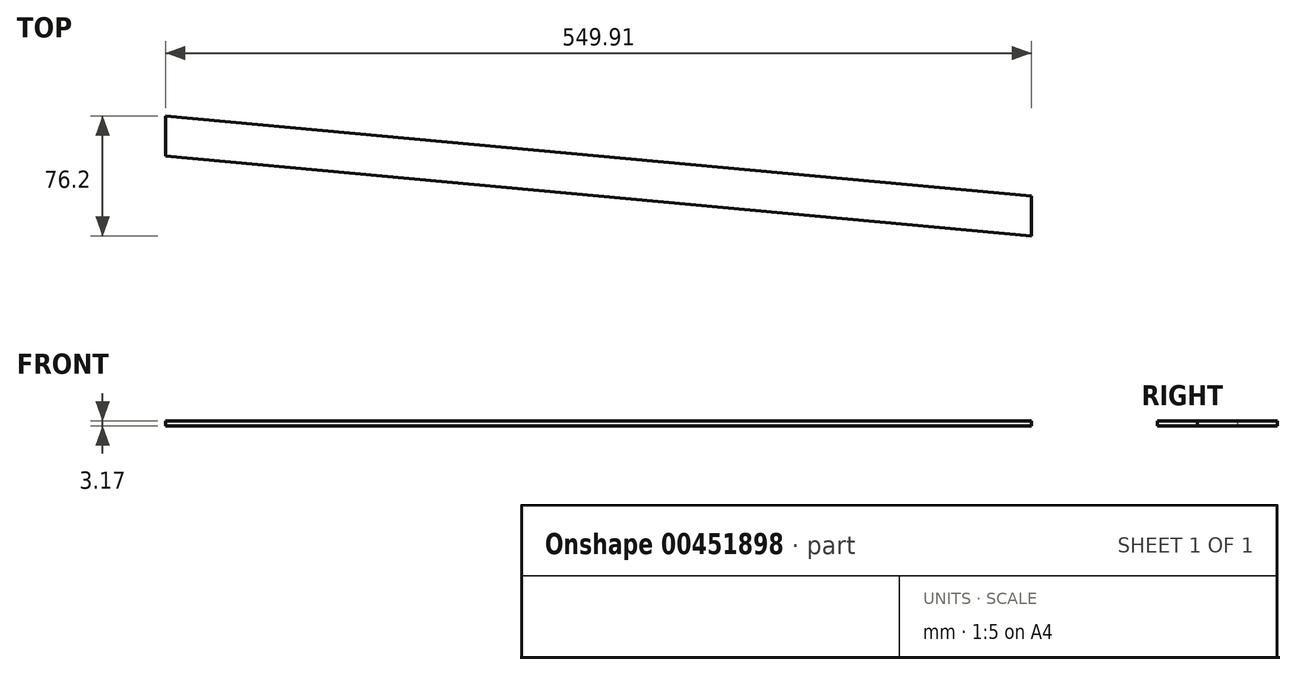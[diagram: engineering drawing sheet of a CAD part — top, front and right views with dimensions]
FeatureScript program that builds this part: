
annotation { "Feature Type Name" : "Feature", "Feature Type Description" : "" }
export const myFeature = defineFeature(function(context is Context, id is Id, definition is map)
    precondition{}
    {
        {
            var Q0;
            Q0=qCreatedBy(makeId("Top.planeOp"),FACE);
            var sketch = newSketch(context, id + "F0", { "sketchPlane" : qUnion([Q0])});
            skLineSegment(sketch, "E0", {"start": v(-200.68, 0.14) * mm, "end": v(-200.68, 139.84) * mm});
            skLineSegment(sketch, "E1", {"start": v(-200.68, 139.84) * mm, "end": v(-195.6, 139.84) * mm});
            skLineSegment(sketch, "E2", {"start": v(-195.6, 139.84) * mm, "end": v(-195.6, 101.74) * mm});
            skLineSegment(sketch, "E3", {"start": v(-195.6, 101.74) * mm, "end": v(460.36, 101.74) * mm, "construction": true});
            skLineSegment(sketch, "E4", {"start": v(-195.6, 101.74) * mm, "end": v(-177.82, 101.74) * mm});
            skLineSegment(sketch, "E5", {"start": v(-200.68, 139.84) * mm, "end": v(460.76, 139.84) * mm, "construction": true});
            skLineSegment(sketch, "E6", {"start": v(-177.82, 101.74) * mm, "end": v(-177.82, 139.84) * mm});
            skLineSegment(sketch, "E7", {"start": v(-177.82, 139.84) * mm, "end": v(-172.74, 139.84) * mm});
            skLineSegment(sketch, "E8", {"start": v(-172.74, 139.84) * mm, "end": v(-172.74, 101.74) * mm});
            skLineSegment(sketch, "E9", {"start": v(-172.74, 101.74) * mm, "end": v(-152.42, 101.74) * mm});
            skLineSegment(sketch, "E10", {"start": v(-152.42, 101.74) * mm, "end": v(-152.42, 139.84) * mm});
            skLineSegment(sketch, "E11", {"start": v(-152.42, 139.84) * mm, "end": v(-147.34, 139.84) * mm});
            skLineSegment(sketch, "E12", {"start": v(-147.34, 139.84) * mm, "end": v(-147.34, 101.74) * mm});
            skLineSegment(sketch, "E13", {"start": v(-147.34, 101.74) * mm, "end": v(-125.75, 101.74) * mm});
            skLineSegment(sketch, "E14", {"start": v(-125.75, 101.74) * mm, "end": v(-125.75, 139.84) * mm});
            skLineSegment(sketch, "E15", {"start": v(-125.75, 139.84) * mm, "end": v(-118.13, 139.84) * mm});
            skLineSegment(sketch, "E16", {"start": v(-118.13, 139.84) * mm, "end": v(-118.13, 101.74) * mm});
            skLineSegment(sketch, "E17", {"start": v(-118.13, 101.74) * mm, "end": v(-96.54, 101.74) * mm});
            skLineSegment(sketch, "E18", {"start": v(-96.54, 101.74) * mm, "end": v(-96.54, 139.84) * mm});
            skLineSegment(sketch, "E19", {"start": v(-96.54, 139.84) * mm, "end": v(-87.65, 139.84) * mm});
            skLineSegment(sketch, "E20", {"start": v(-87.65, 139.84) * mm, "end": v(-87.65, 101.74) * mm});
            skLineSegment(sketch, "E21", {"start": v(-87.65, 101.74) * mm, "end": v(-64.79, 101.74) * mm});
            skLineSegment(sketch, "E22", {"start": v(-64.79, 101.74) * mm, "end": v(-64.79, 139.84) * mm});
            skLineSegment(sketch, "E23", {"start": v(-64.79, 139.84) * mm, "end": v(-54.63, 139.84) * mm});
            skLineSegment(sketch, "E24", {"start": v(-54.63, 139.84) * mm, "end": v(-54.63, 101.74) * mm});
            skLineSegment(sketch, "E25", {"start": v(-54.63, 101.74) * mm, "end": v(-31.77, 101.74) * mm});
            skLineSegment(sketch, "E26", {"start": v(-200.68, 139.84) * mm, "end": v(-200.68, 25.54) * mm, "construction": true});
            skLineSegment(sketch, "E27", {"start": v(-200.68, 25.54) * mm, "end": v(-341.77, 25.54) * mm, "construction": true});
            skLineSegment(sketch, "E28", {"start": v(349.23, -50.66) * mm, "end": v(-200.68, 0.14) * mm});
            skLineSegment(sketch, "E29", {"start": v(-31.77, 101.74) * mm, "end": v(-31.77, 139.84) * mm});
            skLineSegment(sketch, "E30", {"start": v(-31.77, 139.84) * mm, "end": v(-21.6, 139.84) * mm});
            skLineSegment(sketch, "E31", {"start": v(-21.6, 139.84) * mm, "end": v(-21.6, 101.74) * mm});
            skLineSegment(sketch, "E32", {"start": v(-21.6, 101.74) * mm, "end": v(2.52, 101.74) * mm});
            skLineSegment(sketch, "E33", {"start": v(2.52, 101.74) * mm, "end": v(2.52, 139.84) * mm});
            skLineSegment(sketch, "E34", {"start": v(2.52, 139.84) * mm, "end": v(15.22, 139.84) * mm});
            skLineSegment(sketch, "E35", {"start": v(15.22, 139.84) * mm, "end": v(15.22, 101.74) * mm});
            skLineSegment(sketch, "E36", {"start": v(15.22, 101.74) * mm, "end": v(40.62, 101.74) * mm});
            skLineSegment(sketch, "E37", {"start": v(40.62, 101.74) * mm, "end": v(40.62, 139.84) * mm});
            skLineSegment(sketch, "E38", {"start": v(40.62, 139.84) * mm, "end": v(55.86, 139.84) * mm});
            skLineSegment(sketch, "E39", {"start": v(55.86, 139.84) * mm, "end": v(55.86, 101.74) * mm});
            skLineSegment(sketch, "E40", {"start": v(55.86, 101.74) * mm, "end": v(83.8, 101.74) * mm});
            skLineSegment(sketch, "E41", {"start": v(83.8, 101.74) * mm, "end": v(83.8, 139.84) * mm});
            skLineSegment(sketch, "E42", {"start": v(83.8, 139.84) * mm, "end": v(99.04, 139.84) * mm});
            skLineSegment(sketch, "E43", {"start": v(99.04, 139.84) * mm, "end": v(99.04, 101.74) * mm});
            skLineSegment(sketch, "E44", {"start": v(99.04, 101.74) * mm, "end": v(128.25, 101.74) * mm});
            skLineSegment(sketch, "E45", {"start": v(128.25, 101.74) * mm, "end": v(128.25, 139.84) * mm});
            skLineSegment(sketch, "E46", {"start": v(128.25, 139.84) * mm, "end": v(143.5, 139.84) * mm});
            skLineSegment(sketch, "E47", {"start": v(143.5, 139.84) * mm, "end": v(143.5, 101.74) * mm});
            skLineSegment(sketch, "E48", {"start": v(143.5, 101.74) * mm, "end": v(173.97, 101.74) * mm});
            skLineSegment(sketch, "E49", {"start": v(173.97, 101.74) * mm, "end": v(173.97, 139.84) * mm});
            skLineSegment(sketch, "E50", {"start": v(173.97, 139.84) * mm, "end": v(191.75, 139.84) * mm});
            skLineSegment(sketch, "E51", {"start": v(191.75, 139.84) * mm, "end": v(191.75, 101.74) * mm});
            skLineSegment(sketch, "E52", {"start": v(191.75, 101.74) * mm, "end": v(223.5, 101.74) * mm});
            skLineSegment(sketch, "E53", {"start": v(223.5, 101.74) * mm, "end": v(223.5, 139.84) * mm});
            skLineSegment(sketch, "E54", {"start": v(223.5, 139.84) * mm, "end": v(241.28, 139.84) * mm});
            skLineSegment(sketch, "E55", {"start": v(241.28, 139.84) * mm, "end": v(241.28, 101.74) * mm});
            skLineSegment(sketch, "E56", {"start": v(241.28, 101.74) * mm, "end": v(274.3, 101.74) * mm});
            skLineSegment(sketch, "E57", {"start": v(274.3, 101.74) * mm, "end": v(274.3, 139.84) * mm});
            skLineSegment(sketch, "E58", {"start": v(274.3, 139.84) * mm, "end": v(294.62, 139.84) * mm});
            skLineSegment(sketch, "E59", {"start": v(294.62, 139.84) * mm, "end": v(294.62, 101.74) * mm});
            skLineSegment(sketch, "E60", {"start": v(294.62, 101.74) * mm, "end": v(328.91, 101.74) * mm});
            skLineSegment(sketch, "E61", {"start": v(328.91, 101.74) * mm, "end": v(328.91, 139.84) * mm});
            skLineSegment(sketch, "E62", {"start": v(328.91, 139.84) * mm, "end": v(349.23, 139.84) * mm});
            skLineSegment(sketch, "E63", {"start": v(349.23, 139.84) * mm, "end": v(349.23, 101.74) * mm});
            skLineSegment(sketch, "E64", {"start": v(349.23, 101.74) * mm, "end": v(349.23, -50.66) * mm});
            skLineSegment(sketch, "E65", {"start": v(-200.68, 25.54) * mm, "end": v(349.23, -25.26) * mm});
            skSolve(sketch);
        }
        {
            var Q0;
            Q0=makeQuery(id+"F0.imprint","IMPRINT",FACE,{"disambiguationData":[TD([[makeQuery(id+"F0.imprint","IMPRINT",EDGE,{"derivedFrom":sQuery(id+"F0.wireOp",EDGE,"E0")}),-1.0]])]});
            extrude(context, id + "F1", {"entities" : qUnion([Q0]), "depth" : 3.17 * mm});
        }
    });
